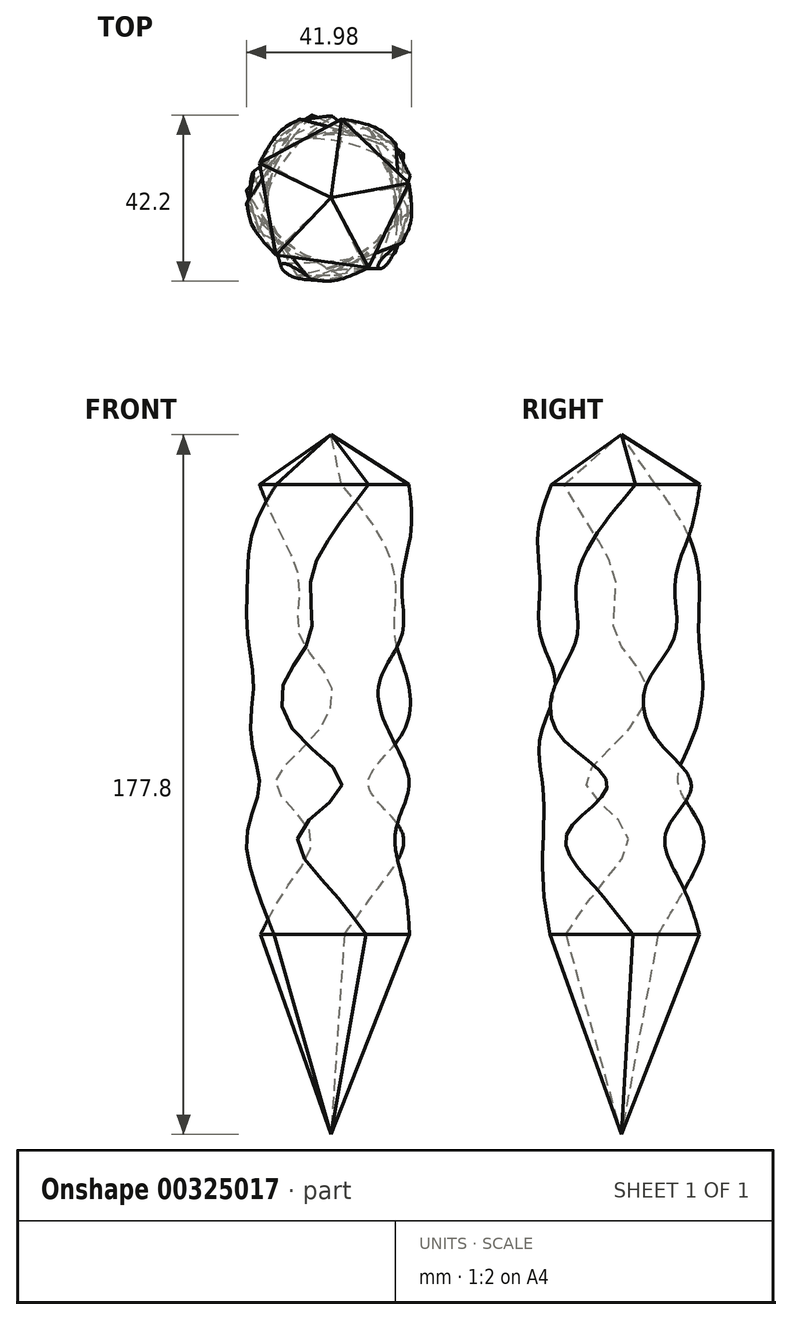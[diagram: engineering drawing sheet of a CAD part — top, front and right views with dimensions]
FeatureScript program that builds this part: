
annotation { "Feature Type Name" : "Feature", "Feature Type Description" : "" }
export const myFeature = defineFeature(function(context is Context, id is Id, definition is map)
    precondition{}
    {
        {
            var Q0;
            Q0=qCreatedBy(makeId("Top.planeOp"),FACE);
            cPlane(context, id + "F0", {"entities" : qUnion([Q0]), "cplaneType" : CPlaneType.OFFSET, "offset" : 12.7 * mm, "width" : 152.4 * mm, "height" : 152.4 * mm});
        }
        {
            var Q0;
            Q0=qCreatedBy(id+"F0.planeOp",FACE);
            cPlane(context, id + "F1", {"entities" : qUnion([Q0]), "cplaneType" : CPlaneType.OFFSET, "offset" : 12.7 * mm, "width" : 152.4 * mm, "height" : 152.4 * mm});
        }
        {
            var Q0;
            Q0=qCreatedBy(id+"F1.planeOp",FACE);
            cPlane(context, id + "F2", {"entities" : qUnion([Q0]), "cplaneType" : CPlaneType.OFFSET, "offset" : 12.7 * mm, "width" : 152.4 * mm, "height" : 152.4 * mm});
        }
        {
            var Q0;
            Q0=qCreatedBy(id+"F2.planeOp",FACE);
            cPlane(context, id + "F3", {"entities" : qUnion([Q0]), "cplaneType" : CPlaneType.OFFSET, "offset" : 12.7 * mm, "width" : 152.4 * mm, "height" : 152.4 * mm});
        }
        {
            var Q0;
            Q0=qCreatedBy(id+"F3.planeOp",FACE);
            cPlane(context, id + "F4", {"entities" : qUnion([Q0]), "cplaneType" : CPlaneType.OFFSET, "offset" : 12.7 * mm, "width" : 152.4 * mm, "height" : 152.4 * mm});
        }
        {
            var Q0;
            Q0=qCreatedBy(id+"F4.planeOp",FACE);
            cPlane(context, id + "F5", {"entities" : qUnion([Q0]), "cplaneType" : CPlaneType.OFFSET, "offset" : 12.7 * mm, "width" : 152.4 * mm, "height" : 152.4 * mm});
        }
        {
            var Q0;
            Q0=qCreatedBy(id+"F5.planeOp",FACE);
            cPlane(context, id + "F6", {"entities" : qUnion([Q0]), "cplaneType" : CPlaneType.OFFSET, "offset" : 12.7 * mm, "width" : 152.4 * mm, "height" : 152.4 * mm});
        }
        {
            var Q0;
            Q0=qCreatedBy(id+"F6.planeOp",FACE);
            cPlane(context, id + "F7", {"entities" : qUnion([Q0]), "cplaneType" : CPlaneType.OFFSET, "offset" : 12.7 * mm, "width" : 152.4 * mm, "height" : 152.4 * mm});
        }
        {
            var Q0;
            Q0=qCreatedBy(id+"F7.planeOp",FACE);
            cPlane(context, id + "F8", {"entities" : qUnion([Q0]), "cplaneType" : CPlaneType.OFFSET, "offset" : 12.7 * mm, "width" : 152.4 * mm, "height" : 152.4 * mm});
        }
        {
            var Q0;
            Q0=qCreatedBy(makeId("Top.planeOp"),FACE);
            var sketch = newSketch(context, id + "F9", { "sketchPlane" : qUnion([Q0])});
            skCircle(sketch, "E0.cCircle", {"center": v(0, 0) * mm, "radius": 16.33 * mm, "construction": true});
            skLineSegment(sketch, "E0.0", {"start": v(-14.44, -14.1) * mm, "end": v(-17.88, 9.38) * mm});
            skLineSegment(sketch, "E0.1", {"start": v(-17.88, 9.38) * mm, "end": v(3.4, 19.9) * mm});
            skLineSegment(sketch, "E0.2", {"start": v(3.4, 19.9) * mm, "end": v(19.97, 2.92) * mm});
            skLineSegment(sketch, "E0.3", {"start": v(19.97, 2.92) * mm, "end": v(8.95, -18.1) * mm});
            skLineSegment(sketch, "E0.4", {"start": v(8.95, -18.1) * mm, "end": v(-14.44, -14.1) * mm});
            skPoint(sketch, "E0.0.midPoint", {"position": v(-16.16, -2.36) * mm});
            skSolve(sketch);
        }
        {
            var Q0;
            Q0=qCreatedBy(id+"F0.planeOp",FACE);
            var sketch = newSketch(context, id + "F10", { "sketchPlane" : qUnion([Q0])});
            skCircle(sketch, "E1.cCircle", {"center": v(0, 0) * mm, "radius": 16.1 * mm, "construction": true});
            skLineSegment(sketch, "E1.0", {"start": v(-1.23, -19.86) * mm, "end": v(-19.27, -4.97) * mm});
            skLineSegment(sketch, "E1.1", {"start": v(-19.27, -4.97) * mm, "end": v(-10.68, 16.79) * mm});
            skLineSegment(sketch, "E1.2", {"start": v(-10.68, 16.79) * mm, "end": v(12.67, 15.35) * mm});
            skLineSegment(sketch, "E1.3", {"start": v(12.67, 15.35) * mm, "end": v(18.5, -7.3) * mm});
            skLineSegment(sketch, "E1.4", {"start": v(18.5, -7.3) * mm, "end": v(-1.23, -19.86) * mm});
            skPoint(sketch, "E1.0.midPoint", {"position": v(-10.25, -12.42) * mm});
            skSolve(sketch);
        }
        {
            var Q0;
            Q0=qCreatedBy(id+"F1.planeOp",FACE);
            var sketch = newSketch(context, id + "F11", { "sketchPlane" : qUnion([Q0])});
            skCircle(sketch, "E2.cCircle", {"center": v(0, 0) * mm, "radius": 17.34 * mm, "construction": true});
            skLineSegment(sketch, "E2.0", {"start": v(-8.2, -19.8) * mm, "end": v(-21.37, 1.67) * mm});
            skLineSegment(sketch, "E2.1", {"start": v(-21.37, 1.67) * mm, "end": v(-5.01, 20.84) * mm});
            skLineSegment(sketch, "E2.2", {"start": v(-5.01, 20.84) * mm, "end": v(18.27, 11.2) * mm});
            skLineSegment(sketch, "E2.3", {"start": v(18.27, 11.2) * mm, "end": v(16.3, -13.91) * mm});
            skLineSegment(sketch, "E2.4", {"start": v(16.3, -13.91) * mm, "end": v(-8.2, -19.8) * mm});
            skPoint(sketch, "E2.0.midPoint", {"position": v(-14.78, -9.07) * mm});
            skSolve(sketch);
        }
        {
            var Q0;
            Q0=qCreatedBy(id+"F2.planeOp",FACE);
            var sketch = newSketch(context, id + "F12", { "sketchPlane" : qUnion([Q0])});
            skCircle(sketch, "E3.cCircle", {"center": v(0, 0) * mm, "radius": 16.31 * mm, "construction": true});
            skLineSegment(sketch, "E3.0", {"start": v(2.77, -19.97) * mm, "end": v(-18.14, -8.8) * mm});
            skLineSegment(sketch, "E3.1", {"start": v(-18.14, -8.8) * mm, "end": v(-13.98, 14.53) * mm});
            skLineSegment(sketch, "E3.2", {"start": v(-13.98, 14.53) * mm, "end": v(9.5, 17.78) * mm});
            skLineSegment(sketch, "E3.3", {"start": v(9.5, 17.78) * mm, "end": v(19.85, -3.54) * mm});
            skLineSegment(sketch, "E3.4", {"start": v(19.85, -3.54) * mm, "end": v(2.77, -19.97) * mm});
            skPoint(sketch, "E3.0.midPoint", {"position": v(-7.69, -14.39) * mm});
            skSolve(sketch);
        }
        {
            var Q0;
            Q0=qCreatedBy(id+"F3.planeOp",FACE);
            var sketch = newSketch(context, id + "F13", { "sketchPlane" : qUnion([Q0])});
            skCircle(sketch, "E4.cCircle", {"center": v(0, -1.77) * mm, "radius": 16.66 * mm, "construction": true});
            skLineSegment(sketch, "E4.0", {"start": v(15.04, -15.84) * mm, "end": v(-8.73, -20.42) * mm});
            skLineSegment(sketch, "E4.1", {"start": v(-8.73, -20.42) * mm, "end": v(-20.43, 0.77) * mm});
            skLineSegment(sketch, "E4.2", {"start": v(-20.43, 0.77) * mm, "end": v(-3.9, 18.44) * mm});
            skLineSegment(sketch, "E4.3", {"start": v(-3.9, 18.44) * mm, "end": v(18.02, 8.18) * mm});
            skLineSegment(sketch, "E4.4", {"start": v(18.02, 8.18) * mm, "end": v(15.04, -15.84) * mm});
            skPoint(sketch, "E4.0.midPoint", {"position": v(3.15, -18.13) * mm});
            skSolve(sketch);
        }
        {
            var Q0;
            Q0=qCreatedBy(id+"F4.planeOp",FACE);
            var sketch = newSketch(context, id + "F14", { "sketchPlane" : qUnion([Q0])});
            skCircle(sketch, "E5.cCircle", {"center": v(0, 0) * mm, "radius": 16.75 * mm, "construction": true});
            skLineSegment(sketch, "E5.0", {"start": v(12.17, -16.75) * mm, "end": v(-12.17, -16.75) * mm});
            skLineSegment(sketch, "E5.1", {"start": v(-12.17, -16.75) * mm, "end": v(-19.7, 6.4) * mm});
            skLineSegment(sketch, "E5.2", {"start": v(-19.7, 6.4) * mm, "end": v(0, 20.7) * mm});
            skLineSegment(sketch, "E5.3", {"start": v(0, 20.7) * mm, "end": v(19.7, 6.4) * mm});
            skLineSegment(sketch, "E5.4", {"start": v(19.7, 6.4) * mm, "end": v(12.17, -16.75) * mm});
            skPoint(sketch, "E5.0.midPoint", {"position": v(0, -16.75) * mm});
            skSolve(sketch);
        }
        {
            var Q0;
            Q0=qCreatedBy(id+"F5.planeOp",FACE);
            var sketch = newSketch(context, id + "F15", { "sketchPlane" : qUnion([Q0])});
            skCircle(sketch, "E6.cCircle", {"center": v(0, 0) * mm, "radius": 17.17 * mm, "construction": true});
            skLineSegment(sketch, "E6.0", {"start": v(-21.17, -1.53) * mm, "end": v(-8, 19.66) * mm});
            skLineSegment(sketch, "E6.1", {"start": v(-8, 19.66) * mm, "end": v(16.23, 13.68) * mm});
            skLineSegment(sketch, "E6.2", {"start": v(16.23, 13.68) * mm, "end": v(18.03, -11.2) * mm});
            skLineSegment(sketch, "E6.3", {"start": v(18.03, -11.2) * mm, "end": v(-5.09, -20.6) * mm});
            skLineSegment(sketch, "E6.4", {"start": v(-5.09, -20.6) * mm, "end": v(-21.17, -1.53) * mm});
            skPoint(sketch, "E6.0.midPoint", {"position": v(-14.58, 9.07) * mm});
            skSolve(sketch);
        }
        {
            var Q0;
            Q0=qCreatedBy(id+"F6.planeOp",FACE);
            var sketch = newSketch(context, id + "F16", { "sketchPlane" : qUnion([Q0])});
            skCircle(sketch, "E7.cCircle", {"center": v(0, 0) * mm, "radius": 17.28 * mm, "construction": true});
            skLineSegment(sketch, "E7.0", {"start": v(-21.31, -1.33) * mm, "end": v(-7.85, 19.86) * mm});
            skLineSegment(sketch, "E7.1", {"start": v(-7.85, 19.86) * mm, "end": v(16.46, 13.6) * mm});
            skLineSegment(sketch, "E7.2", {"start": v(16.46, 13.6) * mm, "end": v(18.03, -11.45) * mm});
            skLineSegment(sketch, "E7.3", {"start": v(18.03, -11.45) * mm, "end": v(-5.32, -20.68) * mm});
            skLineSegment(sketch, "E7.4", {"start": v(-5.32, -20.68) * mm, "end": v(-21.31, -1.33) * mm});
            skPoint(sketch, "E7.0.midPoint", {"position": v(-14.58, 9.26) * mm});
            skSolve(sketch);
        }
        {
            var Q0;
            Q0=qCreatedBy(id+"F7.planeOp",FACE);
            var sketch = newSketch(context, id + "F17", { "sketchPlane" : qUnion([Q0])});
            skCircle(sketch, "E8.cCircle", {"center": v(0, 0) * mm, "radius": 17.14 * mm, "construction": true});
            skLineSegment(sketch, "E8.0", {"start": v(-20.08, -6.76) * mm, "end": v(-12.63, 17) * mm});
            skLineSegment(sketch, "E8.1", {"start": v(-12.63, 17) * mm, "end": v(12.27, 17.27) * mm});
            skLineSegment(sketch, "E8.2", {"start": v(12.27, 17.27) * mm, "end": v(20.22, -6.33) * mm});
            skLineSegment(sketch, "E8.3", {"start": v(20.22, -6.33) * mm, "end": v(0.22, -21.19) * mm});
            skLineSegment(sketch, "E8.4", {"start": v(0.22, -21.19) * mm, "end": v(-20.08, -6.76) * mm});
            skPoint(sketch, "E8.0.midPoint", {"position": v(-16.36, 5.12) * mm});
            skSolve(sketch);
        }
        {
            var Q0;
            Q0=qCreatedBy(id+"F8.planeOp",FACE);
            var sketch = newSketch(context, id + "F18", { "sketchPlane" : qUnion([Q0])});
            skCircle(sketch, "E9.cCircle", {"center": v(0, 0) * mm, "radius": 16.3 * mm, "construction": true});
            skLineSegment(sketch, "E9.0", {"start": v(9.57, -17.73) * mm, "end": v(-13.9, -14.58) * mm});
            skLineSegment(sketch, "E9.1", {"start": v(-13.9, -14.58) * mm, "end": v(-18.17, 8.72) * mm});
            skLineSegment(sketch, "E9.2", {"start": v(-18.17, 8.72) * mm, "end": v(2.68, 19.97) * mm});
            skLineSegment(sketch, "E9.3", {"start": v(2.68, 19.97) * mm, "end": v(19.82, 3.62) * mm});
            skLineSegment(sketch, "E9.4", {"start": v(19.82, 3.62) * mm, "end": v(9.57, -17.73) * mm});
            skPoint(sketch, "E9.0.midPoint", {"position": v(-2.17, -16.16) * mm});
            skSolve(sketch);
        }
        {
            var Q0;
            Q0=makeQuery(id+"F9.imprint","IMPRINT",FACE,{"disambiguationData":[TD([[makeQuery(id+"F9.imprint","IMPRINT",EDGE,{"derivedFrom":sQuery(id+"F9.wireOp",EDGE,"E0.0")}),-1.0]])]});
            var Q1;
            Q1=makeQuery(id+"F10.imprint","IMPRINT",FACE,{"disambiguationData":[TD([[makeQuery(id+"F10.imprint","IMPRINT",EDGE,{"derivedFrom":sQuery(id+"F10.wireOp",EDGE,"E1.0")}),-1.0]])]});
            var Q2;
            Q2=makeQuery(id+"F11.imprint","IMPRINT",FACE,{"disambiguationData":[TD([[makeQuery(id+"F11.imprint","IMPRINT",EDGE,{"derivedFrom":sQuery(id+"F11.wireOp",EDGE,"E2.0")}),-1.0]])]});
            var Q3;
            Q3=makeQuery(id+"F12.imprint","IMPRINT",FACE,{"disambiguationData":[TD([[makeQuery(id+"F12.imprint","IMPRINT",EDGE,{"derivedFrom":sQuery(id+"F12.wireOp",EDGE,"E3.0")}),-1.0]])]});
            var Q4;
            Q4=makeQuery(id+"F13.imprint","IMPRINT",FACE,{"disambiguationData":[TD([[makeQuery(id+"F13.imprint","IMPRINT",EDGE,{"derivedFrom":sQuery(id+"F13.wireOp",EDGE,"E4.0")}),-1.0]])]});
            var Q5;
            Q5=makeQuery(id+"F14.imprint","IMPRINT",FACE,{"disambiguationData":[TD([[makeQuery(id+"F14.imprint","IMPRINT",EDGE,{"derivedFrom":sQuery(id+"F14.wireOp",EDGE,"E5.0")}),-1.0]])]});
            var Q6;
            Q6=makeQuery(id+"F15.imprint","IMPRINT",FACE,{"disambiguationData":[TD([[makeQuery(id+"F15.imprint","IMPRINT",EDGE,{"derivedFrom":sQuery(id+"F15.wireOp",EDGE,"E6.0")}),-1.0]])]});
            var Q7;
            Q7=makeQuery(id+"F16.imprint","IMPRINT",FACE,{"disambiguationData":[TD([[makeQuery(id+"F16.imprint","IMPRINT",EDGE,{"derivedFrom":sQuery(id+"F16.wireOp",EDGE,"E7.0")}),-1.0]])]});
            var Q8;
            Q8=makeQuery(id+"F17.imprint","IMPRINT",FACE,{"disambiguationData":[TD([[makeQuery(id+"F17.imprint","IMPRINT",EDGE,{"derivedFrom":sQuery(id+"F17.wireOp",EDGE,"E8.0")}),-1.0]])]});
            var Q9;
            Q9=makeQuery(id+"F18.imprint","IMPRINT",FACE,{"disambiguationData":[TD([[makeQuery(id+"F18.imprint","IMPRINT",EDGE,{"derivedFrom":sQuery(id+"F18.wireOp",EDGE,"E9.0")}),-1.0]])]});
            loft(context, id + "F19", {"sheetProfilesArray" : [{ "sheetProfileEntities" : qUnion([Q0]) }, { "sheetProfileEntities" : qUnion([Q1]) }, { "sheetProfileEntities" : qUnion([Q2]) }, { "sheetProfileEntities" : qUnion([Q3]) }, { "sheetProfileEntities" : qUnion([Q4]) }, { "sheetProfileEntities" : qUnion([Q5]) }, { "sheetProfileEntities" : qUnion([Q6]) }, { "sheetProfileEntities" : qUnion([Q7]) }, { "sheetProfileEntities" : qUnion([Q8]) }, { "sheetProfileEntities" : qUnion([Q9]) }]});
        }
        {
            var Q0;
            Q0=makeQuery(id+"F19.opLoft","CAP_FACE",FACE,{"disambiguationData":[OSD([makeQuery(id+"F18.imprint","IMPRINT",FACE,{"disambiguationData":[TD([[makeQuery(id+"F18.imprint","IMPRINT",EDGE,{"derivedFrom":sQuery(id+"F18.wireOp",EDGE,"E9.0")}),-1.0]])]})])],"isStart":true});
            cPlane(context, id + "F20", {"entities" : qUnion([Q0]), "cplaneType" : CPlaneType.OFFSET, "offset" : 12.7 * mm, "width" : 152.4 * mm, "height" : 152.4 * mm});
        }
        {
            var Q0;
            Q0=qCreatedBy(id+"F20.planeOp",FACE);
            var sketch = newSketch(context, id + "F21", { "sketchPlane" : qUnion([Q0])});
            skCircle(sketch, "E10", {"center": v(0, 0) * mm, "radius": 6.58 * mm});
            skSolve(sketch);
        }
        {
            var Q1;
            Q1=makeQuery(id+"F19.opLoft","CAP_FACE",FACE,{"disambiguationData":[OSD([makeQuery(id+"F18.imprint","IMPRINT",FACE,{"disambiguationData":[TD([[makeQuery(id+"F18.imprint","IMPRINT",EDGE,{"derivedFrom":sQuery(id+"F18.wireOp",EDGE,"E9.0")}),-1.0]])]})])],"isStart":true});
            var Q2;
            Q2=sQuery(id+"F21.wireOp",VERTEX,"E10.center");
            loft(context, id + "F22", {"operationType" : NewBodyOperationType.ADD, "sheetProfilesArray" : [{ "sheetProfileEntities" : qUnion([Q1]) }, { "sheetProfileEntities" : qUnion([Q2]) }]});
        }
        {
            var Q0;
            Q0=makeQuery(id+"F19.opLoft","CAP_FACE",FACE,{"disambiguationData":[OSD([makeQuery(id+"F9.imprint","IMPRINT",FACE,{"disambiguationData":[TD([[makeQuery(id+"F9.imprint","IMPRINT",EDGE,{"derivedFrom":sQuery(id+"F9.wireOp",EDGE,"E0.0")}),-1.0]])]})])],"isStart":true});
            cPlane(context, id + "F23", {"entities" : qUnion([Q0]), "cplaneType" : CPlaneType.OFFSET, "offset" : 50.8 * mm, "width" : 152.4 * mm, "height" : 152.4 * mm});
        }
        {
            var Q0;
            Q0=qCreatedBy(id+"F23.planeOp",FACE);
            var sketch = newSketch(context, id + "F24", { "sketchPlane" : qUnion([Q0])});
            skCircle(sketch, "E11", {"center": v(0, 0) * mm, "radius": 5.77 * mm});
            skSolve(sketch);
        }
        {
            var Q1;
            Q1=makeQuery(id+"F19.opLoft","CAP_FACE",FACE,{"disambiguationData":[OSD([makeQuery(id+"F9.imprint","IMPRINT",FACE,{"disambiguationData":[TD([[makeQuery(id+"F9.imprint","IMPRINT",EDGE,{"derivedFrom":sQuery(id+"F9.wireOp",EDGE,"E0.0")}),-1.0]])]})])],"isStart":true});
            var Q2;
            Q2=sQuery(id+"F24.wireOp",VERTEX,"E11.center");
            loft(context, id + "F25", {"operationType" : NewBodyOperationType.ADD, "sheetProfilesArray" : [{ "sheetProfileEntities" : qUnion([Q1]) }, { "sheetProfileEntities" : qUnion([Q2]) }]});
        }
    });
